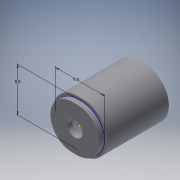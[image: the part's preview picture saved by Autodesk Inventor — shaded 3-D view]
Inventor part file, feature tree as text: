
AUTODESK INVENTOR PART (.ipt)
format: ipt  version: 2016 (Build 200138000, 138)  size: 145,408 bytes
history: native  units: mm
features: sketch x4, extrude x3, hole x1, thicken_offset x1, other x1
ambient origin geometry x8: Origin, YZ Plane, XZ Plane, XY Plane, X Axis, Y Axis, Z Axis, Center Point
bodies: Solid1 (feature_tree)
feature tree (10):
  sketch  "Sketch1"  dims[d2=8.5mm d3=9.5mm]
  extrude  "Extrusion1"  Depth=9.5mm
  hole  "Hole1"  [1 undecoded]
  thicken_offset  "Thicken1"
  sketch  "Sketch2"  dims[d4=12.0mm d5=0.0mm d6=1.0mm d7=0.0mm]
  sketch  "Sketch3"  dims[d8=3.0mm d9=6.0mm d10=4.0mm d11=2.0mm d12=90.0deg d13=8.0mm d14=20.594885mm d15=0.5mm d16=1.0mm]
  extrude  "Extrusion2"  Depth=0.5mm
  other  "Srf1"
  sketch  "Sketch4"  dims[d17=2.0mm d18=1.0mm d19=0.0mm d20=1.5mm d21=1.0mm d22=0.0mm]
  extrude  "ExtrusionSrf1"  Depth=1.0mm
note: 1 required parameter value undecoded (feature->parameter linkage not recoverable at this tier; creation-order binding heuristic only, values carry confidence <= 0.55)
